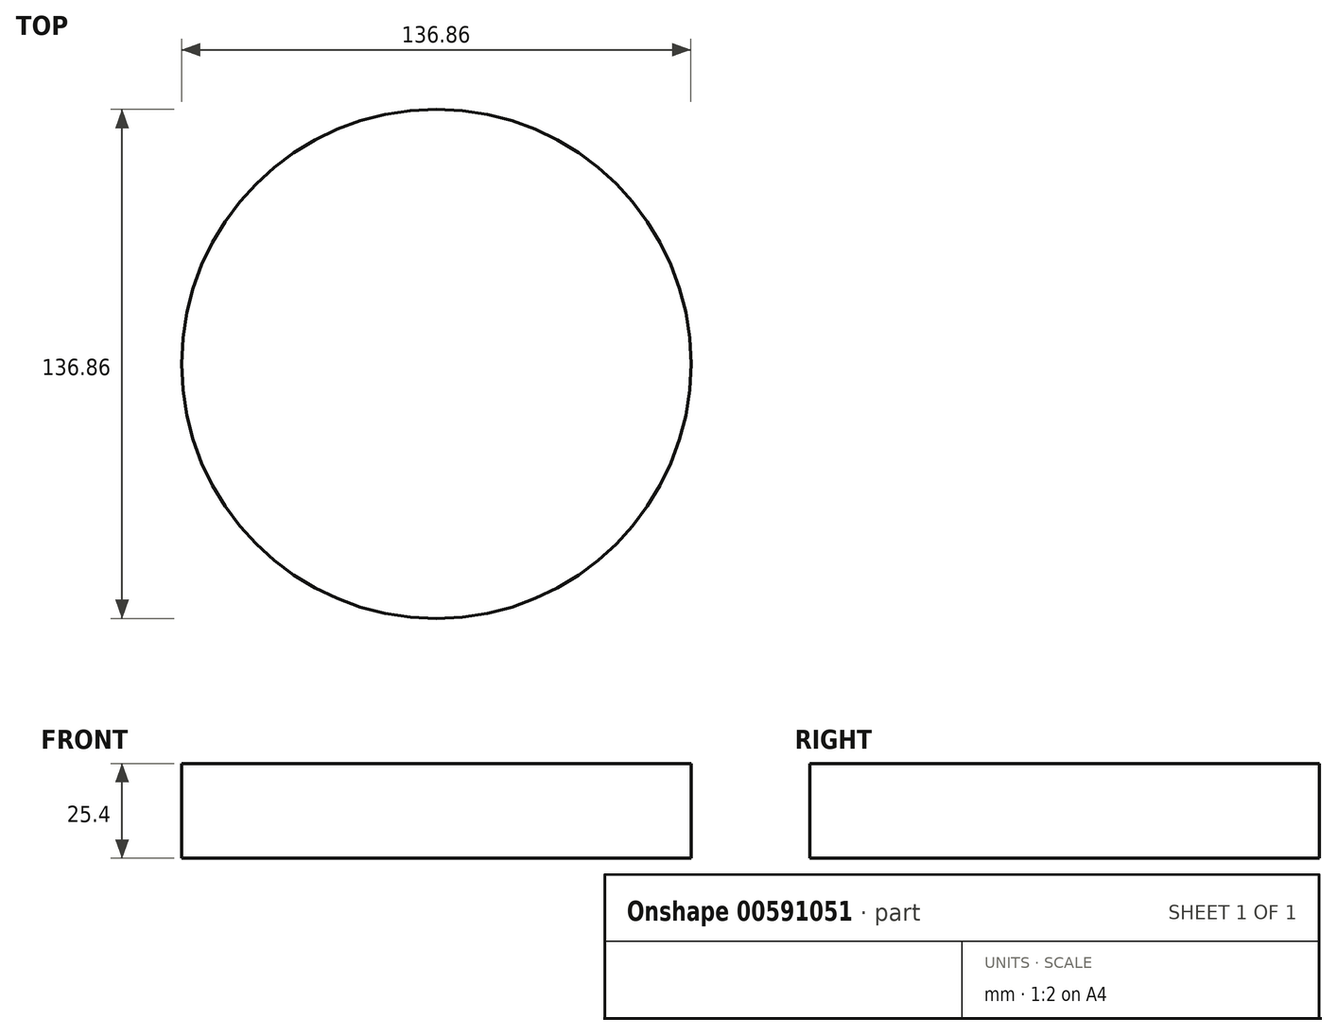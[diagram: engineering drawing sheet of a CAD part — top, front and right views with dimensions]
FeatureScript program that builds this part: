
annotation { "Feature Type Name" : "Feature", "Feature Type Description" : "" }
export const myFeature = defineFeature(function(context is Context, id is Id, definition is map)
    precondition{}
    {
        {
            var Q0;
            Q0=qCreatedBy(makeId("Top.planeOp"),FACE);
            var sketch = newSketch(context, id + "F0", { "sketchPlane" : qUnion([Q0])});
            skCircle(sketch, "E0", {"center": v(0, 0) * mm, "radius": 68.43 * mm});
            skSolve(sketch);
        }
        {
            var Q0;
            Q0=makeQuery(id+"F0.imprint","IMPRINT",FACE,{"disambiguationData":[TD([[makeQuery(id+"F0.imprint","IMPRINT",EDGE,{"derivedFrom":sQuery(id+"F0.wireOp",EDGE,"E0")}),1.0]])]});
            var Q1;
            Q1=sQuery(id+"F0.wireOp",EDGE,"E0");
            extrude(context, id + "F1", {"entities" : qUnion([Q0]), "surfaceEntities" : qUnion([Q1]), "depth" : 25.4 * mm, "offsetDistance" : 25.4 * mm});
        }
    });
